# Revit family: Seating_Inc-Kudl-Metal_Leg-Chair
name_source: partatom
category: Furniture
revit_build: Autodesk Revit 2014 (Build: 20130308_1515(x64)
units: mm (PartAtom-declared; Revit-internal decimal feet)

## types (6) — shared parameters
Assembly Code = E2020200
Depth = 26"
Height = 33 1/2"
Keynote = 12500
Manufacturer = seating inc.
Seat = STI - Fabric
Type Comments = Kudl
URL = http://www.seatinginc.com
Width = 25"

## per-type parameters (varying)
| type | Description | Full Back | Glide | Leg | Model | Open Back |
| Kudl Open Back Black KO4B | Kudl Open Back Black 25"W 26"D 33.5"H | No | STI - Black | STI - Black | KO4B | Yes |
| Kudl Full Back Chrome KF4C | Kudl Full Back Chrome 25"W 26"D 33.5"H | Yes | STI - Chrome | STI - Chrome | KF4C | No |
| Kudl Full Back Silver Metallic KF4SM | Kudl Full Back Silver Metallic 25"W 26"D 33.5"H | Yes | STI - Silver Metallic | STI - Silver Metallic | KF4SM | No |
| Kudl Open Back Chrome KO4C | Kudl Open Back Chrome 25"W 26"D 33.5"H | No | STI - Chrome | STI - Chrome | KO4C | Yes |
| Kudl Open Back Silver Metallic KO4SM | Kudl Open Back Silver Metallic 25"W 26"D 33.5"H | No | STI - Silver Metallic | STI - Silver Metallic | KO4SM | Yes |
| Kudl Full Back  Black KF4B | Kudl Full Back Black 25"W 26"D 33.5"H | Yes | STI - Black | STI - Black | KF4B | No |

## geometry (parser evidence)
native form markers: Sweep x1
no freeform markers — native parametric forms only
